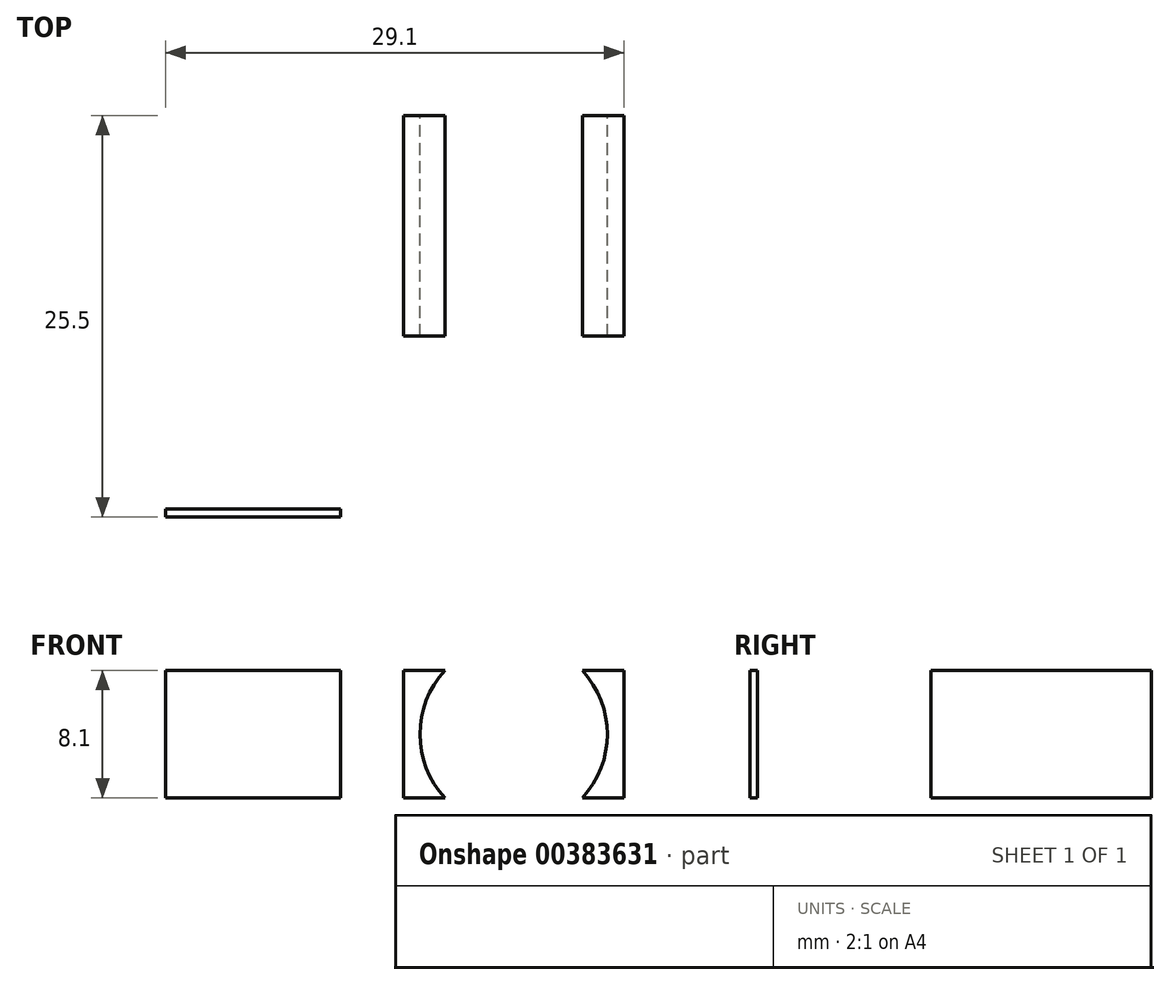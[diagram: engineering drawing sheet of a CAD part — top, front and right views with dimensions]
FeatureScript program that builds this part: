
annotation { "Feature Type Name" : "Feature", "Feature Type Description" : "" }
export const myFeature = defineFeature(function(context is Context, id is Id, definition is map)
    precondition{}
    {
        {
            var Q0;
            Q0=qCreatedBy(makeId("Top.planeOp"),FACE);
            var sketch = newSketch(context, id + "F0", { "sketchPlane" : qUnion([Q0])});
            skLineSegment(sketch, "E0.bottom", {"start": v(0, 0) * mm, "end": v(29.1, 0) * mm});
            skLineSegment(sketch, "E0.top", {"start": v(0, 11.5) * mm, "end": v(29.1, 11.5) * mm});
            skLineSegment(sketch, "E0.left", {"start": v(0, 0) * mm, "end": v(0, 11.5) * mm});
            skLineSegment(sketch, "E0.right", {"start": v(29.1, 0) * mm, "end": v(29.1, 11.5) * mm});
            skLineSegment(sketch, "E1.bottom", {"start": v(29.1, 11.5) * mm, "end": v(15.1, 11.5) * mm});
            skLineSegment(sketch, "E1.top", {"start": v(29.1, 25.5) * mm, "end": v(15.1, 25.5) * mm});
            skLineSegment(sketch, "E1.left", {"start": v(29.1, 11.5) * mm, "end": v(29.1, 25.5) * mm});
            skLineSegment(sketch, "E1.right", {"start": v(15.1, 11.5) * mm, "end": v(15.1, 25.5) * mm});
            skSolve(sketch);
        }
        {
            var Q0;
            Q0 = qSketchRegion(id + "F0", true);
            extrude(context, id + "F1", {"entities" : qUnion([Q0]), "depth" : 8.1 * mm});
        }
        {
            var Q0;
            Q0=makeQuery(id+"F1.opExtrude","SWEPT_FACE",FACE,{"disambiguationData":[OSD([sQuery(id+"F0.wireOp",EDGE,"E0.bottom")])]});
            var sketch = newSketch(context, id + "F2", { "sketchPlane" : qUnion([Q0])});
            skLineSegment(sketch, "E2.bottom", {"start": v(29.1, 8.1) * mm, "end": v(11.1, 8.1) * mm});
            skLineSegment(sketch, "E2.top", {"start": v(29.1, 0) * mm, "end": v(11.1, 0) * mm});
            skLineSegment(sketch, "E2.left", {"start": v(29.1, 8.1) * mm, "end": v(29.1, 0) * mm});
            skLineSegment(sketch, "E2.right", {"start": v(11.1, 8.1) * mm, "end": v(11.1, 0) * mm});
            skLineSegment(sketch, "E3.bottom", {"start": v(11.1, 0) * mm, "end": v(29.1, 0) * mm});
            skLineSegment(sketch, "E3.top", {"start": v(11.1, 0.5) * mm, "end": v(29.1, 0.5) * mm});
            skLineSegment(sketch, "E3.left", {"start": v(11.1, 0) * mm, "end": v(11.1, 0.5) * mm});
            skLineSegment(sketch, "E3.right", {"start": v(29.1, 0) * mm, "end": v(29.1, 0.5) * mm});
            skLineSegment(sketch, "E4.bottom", {"start": v(11.1, 8.1) * mm, "end": v(29.1, 8.1) * mm});
            skLineSegment(sketch, "E4.top", {"start": v(11.1, 7.6) * mm, "end": v(29.1, 7.6) * mm});
            skLineSegment(sketch, "E4.left", {"start": v(11.1, 8.1) * mm, "end": v(11.1, 7.6) * mm});
            skLineSegment(sketch, "E4.right", {"start": v(29.1, 8.1) * mm, "end": v(29.1, 7.6) * mm});
            skSolve(sketch);
        }
        {
            var Q0;
            Q0=makeQuery(id+"F2.imprint","IMPRINT",FACE,{"disambiguationData":[TD([[makeQuery(id+"F2.imprint","IMPRINT",EDGE,{"derivedFrom":sQuery(id+"F2.wireOp",EDGE,"E2.left")}),-1.0]])]});
            extrude(context, id + "F3", {"entities" : qUnion([Q0]), "operationType" : NewBodyOperationType.REMOVE, "oppositeDirection" : true, "depth" : 11.5 * mm});
        }
        {
            var Q0;
            Q0=makeQuery(id+"F1.opExtrude","SWEPT_FACE",FACE,{"disambiguationData":[OSD([sQuery(id+"F0.wireOp",EDGE,"E1.top")])]});
            var sketch = newSketch(context, id + "F4", { "sketchPlane" : qUnion([Q0])});
            skCircle(sketch, "E5", {"center": v(-22.1, 4.05) * mm, "radius": 5.95 * mm});
            skSolve(sketch);
        }
        {
            var Q0;
            {var subQ0=sQuery(id+"F4.wireOp",EDGE,"E5");var subQ1=sQuery(id+"F0.wireOp",EDGE,"E1.top");var subQ2=makeQuery(id+"F1.opExtrude","CAP_EDGE",EDGE,{"disambiguationData":[OSD([subQ1])],"isStart":false});var subQ3=makeQuery(id+"F4.imprint","INTERSECT",VERTEX,{"disambiguationData":[OD(0.0)],"derivedFrom":[subQ2,subQ0]});Q0=makeQuery(id+"F4.imprint","IMPRINT",FACE,{"disambiguationData":[TD([[makeQuery(id+"F4.imprint","IMPRINT",EDGE,{"disambiguationData":[TD([[subQ3,-1.0]])],"derivedFrom":subQ0}),1.0]])]});}
            extrude(context, id + "F5", {"entities" : qUnion([Q0]), "operationType" : NewBodyOperationType.REMOVE, "oppositeDirection" : true, "depth" : 14 * mm});
        }
        {
            var Q0;
            Q0=makeQuery(id+"F1.opExtrude","SWEPT_FACE",FACE,{"disambiguationData":[OSD([sQuery(id+"F0.wireOp",EDGE,"E0.left")])]});
            var sketch = newSketch(context, id + "F6", { "sketchPlane" : qUnion([Q0])});
            skLineSegment(sketch, "E6.bottom", {"start": v(0, 8.1) * mm, "end": v(-0.5, 8.1) * mm});
            skLineSegment(sketch, "E6.top", {"start": v(0, 0) * mm, "end": v(-0.5, 0) * mm});
            skLineSegment(sketch, "E6.left", {"start": v(0, 8.1) * mm, "end": v(0, 0) * mm});
            skLineSegment(sketch, "E6.right", {"start": v(-0.5, 8.1) * mm, "end": v(-0.5, 0) * mm});
            skLineSegment(sketch, "E7.bottom", {"start": v(-11.5, 8.1) * mm, "end": v(-0.5, 8.1) * mm});
            skLineSegment(sketch, "E7.top", {"start": v(-11.5, 7.6) * mm, "end": v(-0.5, 7.6) * mm});
            skLineSegment(sketch, "E7.left", {"start": v(-11.5, 8.1) * mm, "end": v(-11.5, 7.6) * mm});
            skLineSegment(sketch, "E7.right", {"start": v(-0.5, 8.1) * mm, "end": v(-0.5, 7.6) * mm});
            skLineSegment(sketch, "E8.bottom", {"start": v(-11.5, 0) * mm, "end": v(-0.5, 0) * mm});
            skLineSegment(sketch, "E8.top", {"start": v(-11.5, 0.5) * mm, "end": v(-0.5, 0.5) * mm});
            skLineSegment(sketch, "E8.left", {"start": v(-11.5, 0) * mm, "end": v(-11.5, 0.5) * mm});
            skLineSegment(sketch, "E8.right", {"start": v(-0.5, 0) * mm, "end": v(-0.5, 0.5) * mm});
            skSolve(sketch);
        }
        {
            var Q0;
            {var subQ0=sQuery(id+"F6.wireOp",EDGE,"E6.right");Q0=makeQuery(id+"F6.imprint","IMPRINT",FACE,{"disambiguationData":[TD([[makeQuery(id+"F6.imprint","IMPRINT",EDGE,{"derivedFrom":subQ0}),-1.0]])]});}
            extrude(context, id + "F7", {"entities" : qUnion([Q0]), "operationType" : NewBodyOperationType.REMOVE, "oppositeDirection" : true, "depth" : 25 * mm});
        }
    });
